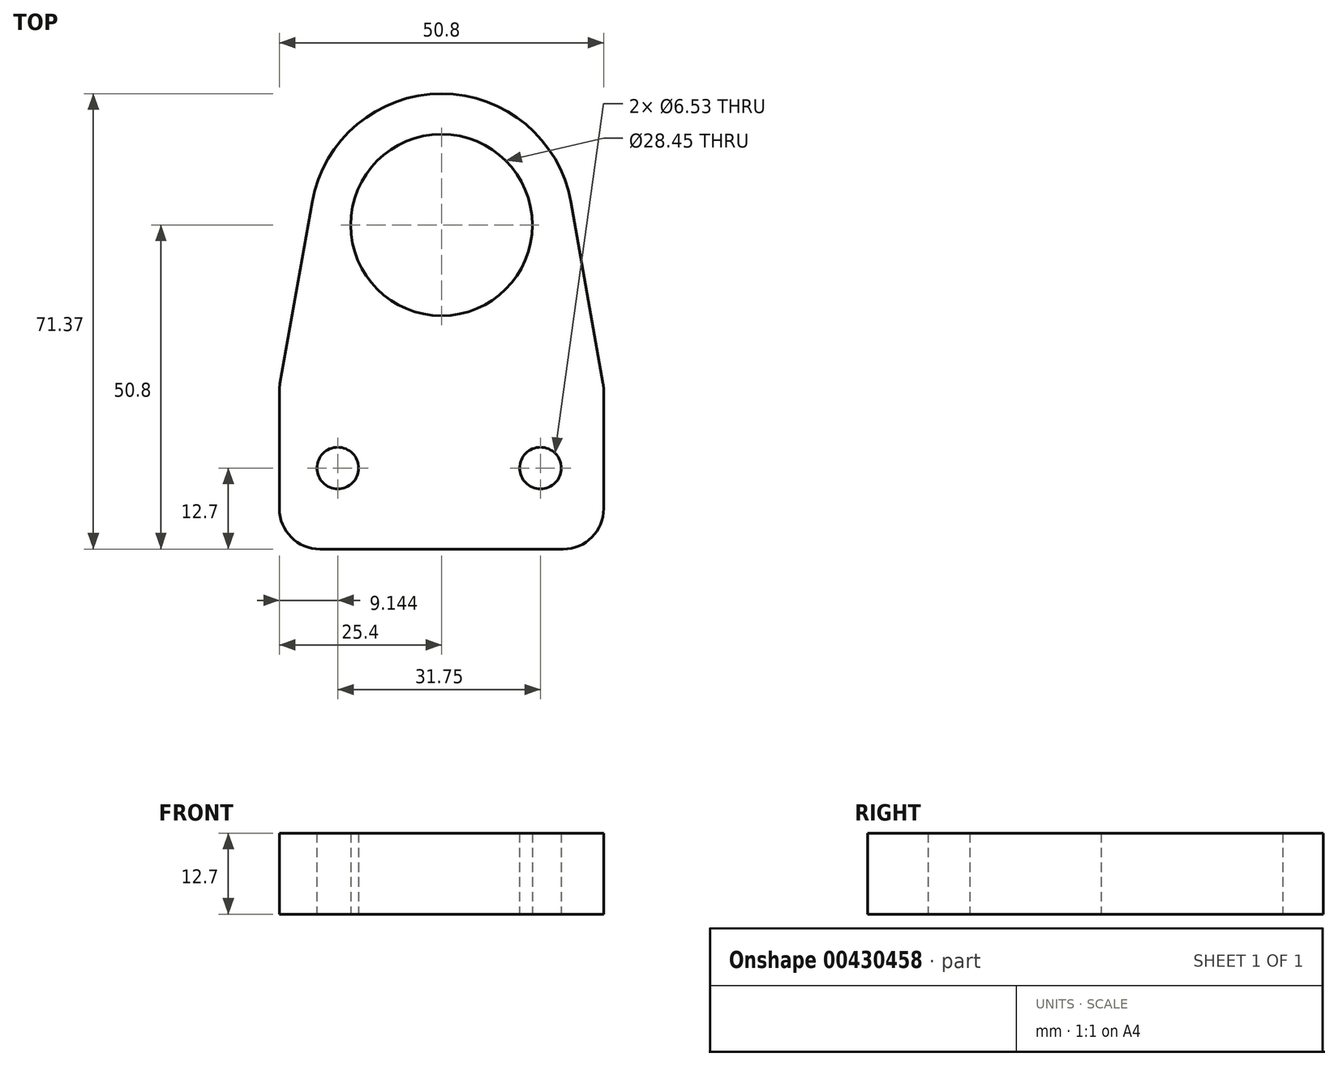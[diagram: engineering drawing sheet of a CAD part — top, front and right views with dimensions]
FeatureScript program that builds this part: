
annotation { "Feature Type Name" : "Feature", "Feature Type Description" : "" }
export const myFeature = defineFeature(function(context is Context, id is Id, definition is map)
    precondition{}
    {
        {
            var Q0;
            Q0=qCreatedBy(makeId("Top.planeOp"),FACE);
            var sketch = newSketch(context, id + "F0", { "sketchPlane" : qUnion([Q0])});
            skLineSegment(sketch, "E0.bottom", {"start": v(19.05, -12.7) * mm, "end": v(-19.05, -12.7) * mm});
            skLineSegment(sketch, "E0.left", {"start": v(25.4, -6.35) * mm, "end": v(25.4, 12.7) * mm});
            skLineSegment(sketch, "E0.right", {"start": v(-25.4, -6.35) * mm, "end": v(-25.4, 12.7) * mm});
            skPoint(sketch, "E0.middle", {"position": v(0, 0) * mm});
            skLineSegment(sketch, "E1", {"start": v(0, 0) * mm, "end": v(0, -12.7) * mm, "construction": true});
            skLineSegment(sketch, "E2", {"start": v(-25.4, 0) * mm, "end": v(25.4, 0) * mm, "construction": true});
            skPoint(sketch, "E3", {"position": v(-16.26, 0) * mm});
            skPoint(sketch, "E4", {"position": v(15.5, 0) * mm});
            skCircle(sketch, "E5", {"center": v(-16.26, 0) * mm, "radius": 3.26 * mm});
            skCircle(sketch, "E6", {"center": v(15.5, 0) * mm, "radius": 3.26 * mm});
            skCircle(sketch, "E7", {"center": v(0, 38.1) * mm, "radius": 14.22 * mm});
            skArc(sketch, "E8", {"start": v(20.26, 41.7) * mm, "mid": v(0, 58.67) * mm, "end": v(-20.26, 41.7) * mm});
            skLineSegment(sketch, "E9", {"start": v(-20.26, 41.7) * mm, "end": v(-25.4, 12.7) * mm});
            skLineSegment(sketch, "E10.MirrorCS", {"start": v(20.26, 41.7) * mm, "end": v(25.4, 12.7) * mm});
            skPoint(sketch, "E11.visualSharp", {"position": v(-25.4, -12.7) * mm});
            skArc(sketch, "E11.filletArc", {"start": v(-25.4, -6.35) * mm, "mid": v(-23.54, -10.84) * mm, "end": v(-19.05, -12.7) * mm});
            skPoint(sketch, "E12.visualSharp", {"position": v(25.4, -12.7) * mm});
            skArc(sketch, "E12.filletArc", {"start": v(19.05, -12.7) * mm, "mid": v(23.54, -10.84) * mm, "end": v(25.4, -6.35) * mm});
            skLineSegment(sketch, "E13", {"start": v(-25.4, 12.7) * mm, "end": v(25.4, 12.7) * mm, "construction": true});
            skSolve(sketch);
        }
        {
            var Q0;
            Q0=makeQuery(id+"F0.imprint","IMPRINT",FACE,{"disambiguationData":[TD([[makeQuery(id+"F0.imprint","IMPRINT",EDGE,{"derivedFrom":sQuery(id+"F0.wireOp",EDGE,"E0.bottom")}),-1.0]])]});
            extrude(context, id + "F1", {"entities" : qUnion([Q0]), "depth" : 12.7 * mm});
        }
        {
            var Q0;
            Q0=makeQuery(id+"F1.opExtrude","SWEPT_EDGE",EDGE,{"disambiguationData":[OSD([sQuery(id+"F0.wireOp",EDGE,"E0.left"),sQuery(id+"F0.wireOp",EDGE,"E10.MirrorCS")])]});
            var Q1;
            Q1=makeQuery(id+"F1.opExtrude","SWEPT_EDGE",EDGE,{"disambiguationData":[OSD([sQuery(id+"F0.wireOp",EDGE,"E0.right"),sQuery(id+"F0.wireOp",EDGE,"E9")])]});
            fillet(context, id + "F2", {"entities" : qUnion([Q0, Q1]), "radius" : 6.35 * mm, "tangentPropagation" : true, "allowEdgeOverflow" : false});
        }
    });
